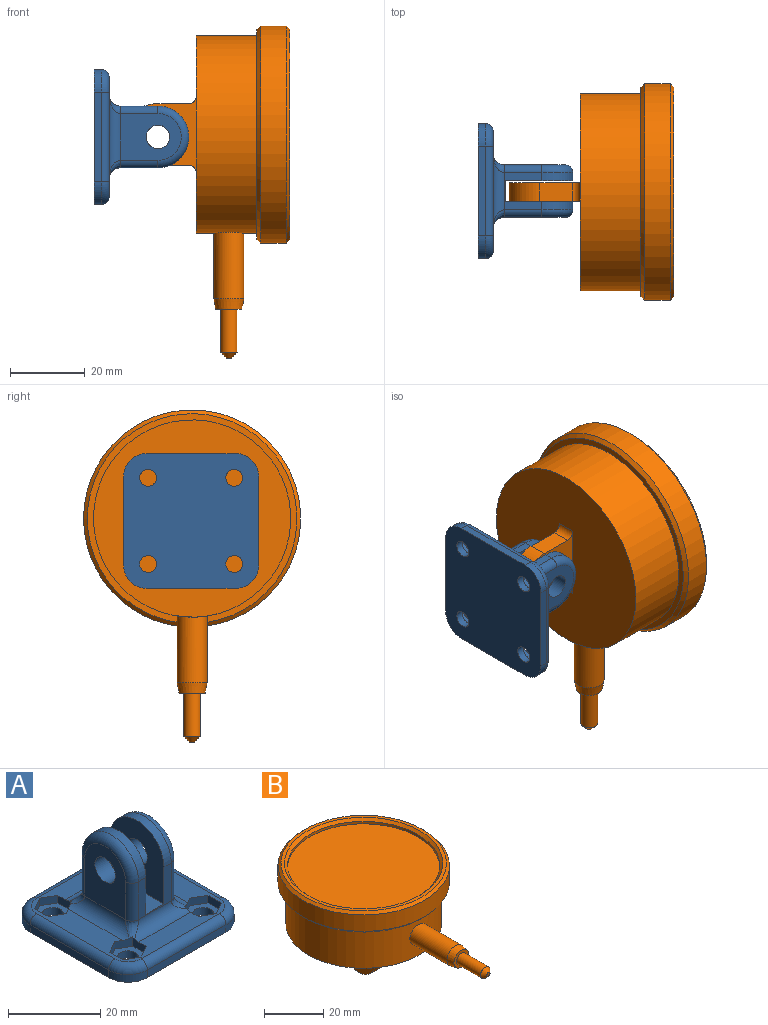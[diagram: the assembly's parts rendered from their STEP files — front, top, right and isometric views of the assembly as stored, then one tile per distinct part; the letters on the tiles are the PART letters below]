
ASSEMBLY  parts=2 mates=1
PART A: 75 faces, bbox 37x37x26 mm
  f0: plane 16.3x12.5mm, normal (1,0,0), area 155.8mm2, adj f51,f55,f71,f72,f73
  f1: plane 16.3x12.5mm, normal (-1,0,0), area 155.8mm2, adj f48,f53,f66,f67,f68
  f2: plane 18x16.5mm, normal (-1,0,0), area 236.6mm2, adj f4,f47,f52,f55,f56
  f3: plane 18x16.5mm, normal (1,0,0), area 236.6mm2, adj f4,f47,f52,f53,f54
  f4: plane 10.05x10mm, normal (0,-1,0), area 46.9mm2, adj f2,f3,f49,f52,f54,f56,f66,f71
  f5: plane 3.6x2.54mm, normal (0.5,0.87,0), area 8.7mm2, adj f6,f36,f37,f46,f51,f74
  f6: plane 4.15x2.54mm, normal (1,0,0), area 8.5mm2, adj f5,f7,f37,f46,f50,f74
  f7: plane 3.55x2.05mm, normal (0.5,-0.87,0), area 8.2mm2, adj f6,f8,f37,f46
  f8: plane 3.55x2.05mm, normal (-0.5,-0.87,0), area 8.2mm2, adj f7,f9,f37,f46
  f9: plane 4.1x2mm, normal (-1,0,0), area 8.2mm2, adj f8,f36,f37,f46
  f10: plane 3.55x2.05mm, normal (0.5,0.87,0), area 8.2mm2, adj f11,f32,f37,f42
  f11: plane 4.15x2.54mm, normal (1,0,0), area 8.5mm2, adj f10,f12,f37,f42,f49,f70
  f12: plane 3.6x2.54mm, normal (0.5,-0.87,0), area 8.7mm2, adj f11,f13,f37,f42,f51,f70
  f13: plane 3.55x2.05mm, normal (-0.5,-0.87,0), area 8.2mm2, adj f12,f14,f37,f42
  f14: plane 4.1x2mm, normal (-1,0,0), area 8.2mm2, adj f13,f32,f37,f42
  f15: plane 3.55x2.05mm, normal (-0.5,-0.87,0), area 8.2mm2, adj f16,f33,f37,f44
  f16: plane 4.15x2.54mm, normal (-1,0,0), area 8.5mm2, adj f15,f17,f37,f44,f50,f69
  f17: plane 3.6x2.54mm, normal (-0.5,0.87,0), area 8.7mm2, adj f16,f18,f37,f44,f48,f69
  f18: plane 3.55x2.05mm, normal (0.5,0.87,0), area 8.2mm2, adj f17,f19,f37,f44
  f19: plane 4.1x2mm, normal (1,0,0), area 8.2mm2, adj f18,f33,f37,f44
  f20: plane 3.6x2.54mm, normal (-0.5,-0.87,0), area 8.7mm2, adj f21,f34,f37,f40,f48,f65
  f21: plane 4.15x2.54mm, normal (-1,0,0), area 8.5mm2, adj f20,f22,f37,f40,f49,f65
  f22: plane 3.55x2.05mm, normal (-0.5,0.87,0), area 8.2mm2, adj f21,f23,f37,f40
  f23: plane 3.55x2.05mm, normal (0.5,0.87,0), area 8.2mm2, adj f22,f24,f37,f40
  f24: plane 4.1x2mm, normal (1,0,0), area 8.2mm2, adj f23,f34,f37,f40
  f25: plane 24x2mm, normal (0,-1,0), area 48mm2, adj f26,f35,f38,f61
  f26: cylinder r=6mm len=6mm, axis (0,0,-1), area 18.8mm2, adj f25,f27,f38,f59
  f27: plane 24x2mm, normal (1,0,0), area 48mm2, adj f26,f28,f38,f57
  f28: cylinder r=6mm len=6mm, axis (0,0,-1), area 18.8mm2, adj f27,f29,f38,f58
  f29: plane 24x2mm, normal (0,1,0), area 48mm2, adj f28,f30,f38,f60
  f30: cylinder r=6mm len=6mm, axis (0,0,-1), area 18.8mm2, adj f29,f31,f38,f62
  f31: plane 24x2mm, normal (-1,0,0), area 48mm2, adj f30,f35,f38,f64
  f32: plane 3.55x2.05mm, normal (-0.5,0.87,0), area 8.2mm2, adj f10,f14,f37,f42
  f33: plane 3.55x2.05mm, normal (0.5,-0.87,0), area 8.2mm2, adj f15,f19,f37,f44
  f34: plane 3.55x2.05mm, normal (0.5,-0.87,0), area 8.2mm2, adj f20,f24,f37,f40
  f35: cylinder r=6mm len=6mm, axis (0,0,-1), area 18.8mm2, adj f25,f31,f38,f63
  f36: plane 3.55x2.05mm, normal (-0.5,0.87,0), area 8.2mm2, adj f5,f9,f37,f46
  f37: plane 32x32mm, normal (0,0,1), area 405.2mm2, adj f5,f6,f7,f8,f9,f10,f11,f12
  f38: plane 36x36mm, normal (0,0,-1), area 1201.5mm2, adj f25,f26,f27,f28,f29,f30,f31,f35
  f39: cylinder r=2.25mm len=4.5mm, axis (0,0,-1), area 28.3mm2, adj f38,f40
  f40: plane 8.2x7.1mm, normal (0,0,1), area 27.8mm2, adj f20,f21,f22,f23,f24,f34,f39
  f41: cylinder r=2.25mm len=4.5mm, axis (0,0,-1), area 28.3mm2, adj f38,f42
  f42: plane 8.2x7.1mm, normal (0,0,1), area 27.8mm2, adj f10,f11,f12,f13,f14,f32,f41
  f43: cylinder r=2.25mm len=4.5mm, axis (0,0,-1), area 28.3mm2, adj f38,f44
  f44: plane 8.2x7.1mm, normal (0,0,1), area 27.8mm2, adj f15,f16,f17,f18,f19,f33,f43
  f45: cylinder r=2.25mm len=4.5mm, axis (0,0,-1), area 28.3mm2, adj f38,f46
  f46: plane 8.2x7.1mm, normal (0,0,1), area 27.8mm2, adj f5,f6,f7,f8,f9,f36,f45
  f47: plane 10.05x10mm, normal (0,1,0), area 46.9mm2, adj f2,f3,f50,f52,f54,f56,f68,f73
  f48: cylinder r=3mm len=18.07mm, axis (0,1,0), area 74.8mm2, adj f1,f17,f20,f37,f65,f69
  f49: cylinder r=3mm len=15.9mm, axis (-1,0,0), area 61.7mm2, adj f4,f11,f21,f37,f65,f70
  f50: cylinder r=3mm len=15.9mm, axis (1,0,0), area 61.7mm2, adj f6,f16,f37,f47,f69,f74
  f51: cylinder r=3mm len=18.07mm, axis (0,-1,0), area 74.8mm2, adj f0,f5,f12,f37,f70,f74
  f52: plane 16.5x5.5mm, normal (0,0,1), area 90.7mm2, adj f2,f3,f4,f47
  f53: cylinder r=3.15mm len=6.3mm, axis (1,0,0), area 84.1mm2, adj f1,f3
  f54: cylinder r=8.25mm len=16.5mm, axis (1,0,0), area 58.3mm2, adj f3,f4,f47,f67
  f55: cylinder r=3.15mm len=6.3mm, axis (1,0,0), area 84.1mm2, adj f0,f2
  f56: cylinder r=8.25mm len=16.5mm, axis (1,0,0), area 58.3mm2, adj f2,f4,f47,f72
  f57: cylinder r=2mm len=24mm, axis (0,-1,0), area 75.4mm2, adj f27,f37,f58,f59
  f58: torus R=4mm, axis (0,0,1), area 26mm2, adj f28,f37,f57,f60
  f59: torus R=4mm, axis (0,0,1), area 26mm2, adj f26,f37,f57,f61
  f60: cylinder r=2mm len=24mm, axis (1,0,0), area 75.4mm2, adj f29,f37,f58,f62
  f61: cylinder r=2mm len=24mm, axis (-1,0,0), area 75.4mm2, adj f25,f37,f59,f63
  f62: torus R=4mm, axis (0,0,1), area 26mm2, adj f30,f37,f60,f64
  f63: torus R=4mm, axis (0,0,1), area 26mm2, adj f35,f37,f61,f64
  f64: cylinder r=2mm len=24mm, axis (0,1,0), area 75.4mm2, adj f31,f37,f62,f63
  f65: bspline ~3.94x3.94mm, area 9.3mm2, adj f20,f21,f48,f49,f66
  f66: cylinder r=2mm len=10.05mm, axis (0,0,1), area 31.6mm2, adj f1,f4,f65,f67
  f67: torus R=6.25mm, axis (1,0,0), area 74.3mm2, adj f1,f54,f66,f68
  f68: cylinder r=2mm len=10.05mm, axis (0,0,-1), area 31.6mm2, adj f1,f47,f67,f69
  f69: bspline ~3.94x3.94mm, area 9.3mm2, adj f16,f17,f48,f50,f68
  f70: bspline ~3.94x3.94mm, area 9.3mm2, adj f11,f12,f49,f51,f71
  f71: cylinder r=2mm len=10.05mm, axis (0,0,-1), area 31.6mm2, adj f0,f4,f70,f72
  f72: torus R=6.25mm, axis (1,0,0), area 74.3mm2, adj f0,f56,f71,f73
  f73: cylinder r=2mm len=10.05mm, axis (0,0,1), area 31.6mm2, adj f0,f47,f72,f74
  f74: bspline ~3.94x3.94mm, area 9.3mm2, adj f5,f6,f50,f51,f73
PART B: 24 faces, bbox 58x88.7x44 mm
  f0: cylinder r=26.35mm len=52.7mm, axis (0,0,-1), area 2631.6mm2, adj f1,f4,f12
  f1: plane 52.7x52.7mm, normal (0,0,-1), area 2079.3mm2, adj f0,f5,f7,f17,f18
  f2: cylinder r=29mm len=58mm, axis (0,0,-1), area 1239mm2, adj f21,f22
  f3: plane 56x56mm, normal (0,0,1), area 206.6mm2, adj f22,f23
  f4: plane 56x56mm, normal (0,0,-1), area 281.7mm2, adj f0,f21
  f5: plane 20.4x19mm, normal (1,0,0), area 251.3mm2, adj f1,f6,f8,f9,f10,f17,f18
  f6: plane 8.8x5mm, normal (0,1,0), area 44mm2, adj f5,f7,f9,f17
  f7: plane 20.4x19mm, normal (-1,0,0), area 251.3mm2, adj f1,f6,f8,f9,f10,f17,f18
  f8: plane 8.8x5mm, normal (0,-1,0), area 44mm2, adj f5,f7,f9,f18
  f9: cylinder r=8.2mm len=16.4mm, axis (1,0,0), area 128.8mm2, adj f5,f6,f7,f8
  f10: cylinder r=3.25mm len=6.5mm, axis (1,0,0), area 102.1mm2, adj f5,f7
  f11: plane 7x7mm, normal (0,-1,0), area 22.6mm2, adj f14,f16
  f12: cylinder r=4mm len=17.82mm, axis (0,1,0), area 444mm2, adj f0,f16
  f13: plane 1.5x1.5mm, normal (0,-1,0), area 1.8mm2, adj f15
  f14: cylinder r=2.25mm len=11.5mm, axis (0,1,0), area 162.6mm2, adj f11,f15
  f15: cone r=0.75mm half-angle=45deg, axis (0,1,0), area 20mm2, adj f13,f14
  f16: cone r=3.5mm half-angle=10deg, axis (0,1,0), area 67.8mm2, adj f11,f12
  f17: cylinder r=2mm len=5mm, axis (-1,0,0), area 15.7mm2, adj f1,f5,f6,f7
  f18: cylinder r=2mm len=5mm, axis (1,0,0), area 15.7mm2, adj f1,f5,f7,f8
  f19: cylinder r=25.8mm len=51.6mm, axis (0,0,1), area 162.1mm2, adj f20,f23
  f20: plane 51.6x51.6mm, normal (0,0,1), area 2091.2mm2, adj f19
  f21: cone r=29mm half-angle=45deg, axis (0,0,1), area 253.2mm2, adj f2,f4
  f22: cone r=28mm half-angle=45deg, axis (0,0,-1), area 253.2mm2, adj f2,f3
  f23: cone r=25.8mm half-angle=45deg, axis (0,0,1), area 233.7mm2, adj f3,f19
PLACE A rot(axis=(0.58,0.58,0.58),120deg) t=(-36,0.25,59.05)mm
PLACE B rot(axis=(0.58,0.58,0.58),120deg) t=(-8.7,0,59.7)mm
MATE fastened A.f53 <-> B.f10  axis (0,1,0) through (-18.95,-2.5,59.05)mm
